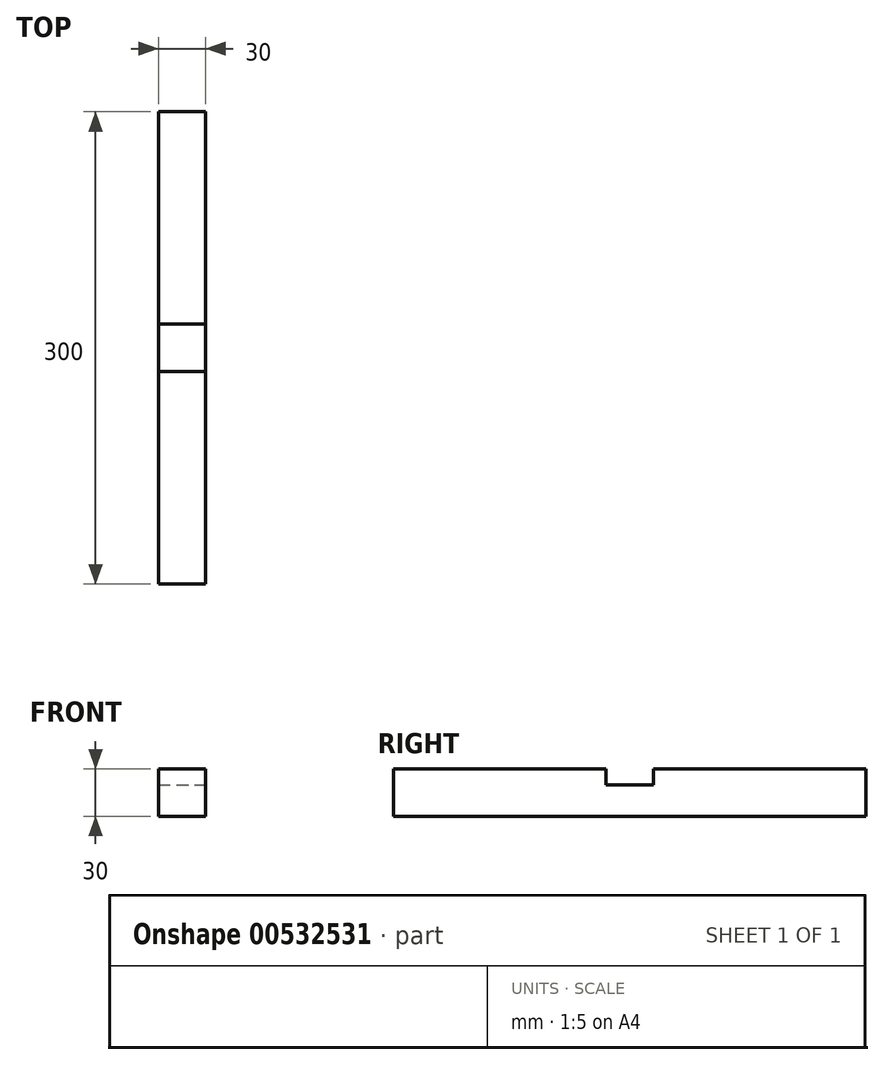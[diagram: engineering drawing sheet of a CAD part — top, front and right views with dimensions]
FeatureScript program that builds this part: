
annotation { "Feature Type Name" : "Feature", "Feature Type Description" : "" }
export const myFeature = defineFeature(function(context is Context, id is Id, definition is map)
    precondition{}
    {
        {
            var Q0;
            Q0=qCreatedBy(makeId("Top.planeOp"),FACE);
            var sketch = newSketch(context, id + "F0", { "sketchPlane" : qUnion([Q0])});
            skLineSegment(sketch, "E0.bottom", {"start": v(-30.29, 165) * mm, "end": v(-0.29, 165) * mm});
            skLineSegment(sketch, "E0.top", {"start": v(-30.29, -135) * mm, "end": v(-0.29, -135) * mm});
            skLineSegment(sketch, "E0.left", {"start": v(-30.29, 165) * mm, "end": v(-30.29, -135) * mm});
            skLineSegment(sketch, "E0.right", {"start": v(-0.29, 165) * mm, "end": v(-0.29, -135) * mm});
            skLineSegment(sketch, "E1", {"start": v(-30.29, 165) * mm, "end": v(-30.29, 30) * mm});
            skLineSegment(sketch, "E2", {"start": v(-30.29, -135) * mm, "end": v(-30.29, 30) * mm});
            skLineSegment(sketch, "E3", {"start": v(-30.29, -135) * mm, "end": v(-30.29, 0) * mm});
            skLineSegment(sketch, "E4", {"start": v(-0.29, 30) * mm, "end": v(0, 0) * mm});
            skSolve(sketch);
        }
        {
            var Q0;
            {var subQ3=sQuery(id+"F0.wireOp",EDGE,"E0.bottom");Q0=makeQuery(id+"F0.imprint","IMPRINT",FACE,{"disambiguationData":[TD([[makeQuery(id+"F0.imprint","IMPRINT",EDGE,{"derivedFrom":subQ3}),-1.0]])]});}
            extrude(context, id + "F1", {"entities" : qUnion([Q0]), "depth" : 20 * mm, "offsetDistance" : 25 * mm});
        }
        {
            var Q0;
            Q0=makeQuery(id+"F1.opExtrude","CAP_FACE",FACE,{"disambiguationData":[OSD([sQuery(id+"F0.wireOp",EDGE,"E0.bottom"),sQuery(id+"F0.wireOp",EDGE,"E0.top"),sQuery(id+"F0.wireOp",EDGE,"E0.right"),sQuery(id+"F0.wireOp",EDGE,"E1"),sQuery(id+"F0.wireOp",EDGE,"E2"),sQuery(id+"F0.wireOp",EDGE,"E3")])],"isStart":false});
            var sketch = newSketch(context, id + "F2", { "sketchPlane" : qUnion([Q0])});
            skLineSegment(sketch, "E5", {"start": v(0, 30) * mm, "end": v(-30.29, 30) * mm});
            skPoint(sketch, "E5.startSnap0", {"position": v(-30.29, 15) * mm});
            skLineSegment(sketch, "E6", {"start": v(-30.29, 30) * mm, "end": v(-30.29, 0) * mm});
            skLineSegment(sketch, "E7", {"start": v(-30.29, 0) * mm, "end": v(-0.29, 0) * mm});
            skLineSegment(sketch, "E8", {"start": v(-0.29, 0) * mm, "end": v(0, 30) * mm});
            skSolve(sketch);
        }
        {
            var Q0;
            {var subQ0=sQuery(id+"F2.wireOp",EDGE,"E7");Q0=makeQuery(id+"F2.imprint","IMPRINT",FACE,{"disambiguationData":[TD([[makeQuery(id+"F2.imprint","IMPRINT",EDGE,{"derivedFrom":subQ0}),-1.0]])]});}
            var Q1;
            {var subQ5=makeQuery(id+"F1.opExtrude","CAP_EDGE",EDGE,{"disambiguationData":[OSD([sQuery(id+"F0.wireOp",EDGE,"E0.bottom")])],"isStart":false});Q1=makeQuery(id+"F2.imprint","IMPRINT",FACE,{"disambiguationData":[TD([[makeQuery(id+"F2.imprint","IMPRINT",EDGE,{"derivedFrom":subQ5}),-1.0]])]});}
            extrude(context, id + "F3", {"entities" : qUnion([Q0, Q1]), "operationType" : NewBodyOperationType.ADD, "depth" : 10 * mm, "offsetDistance" : 25 * mm});
        }
    });
